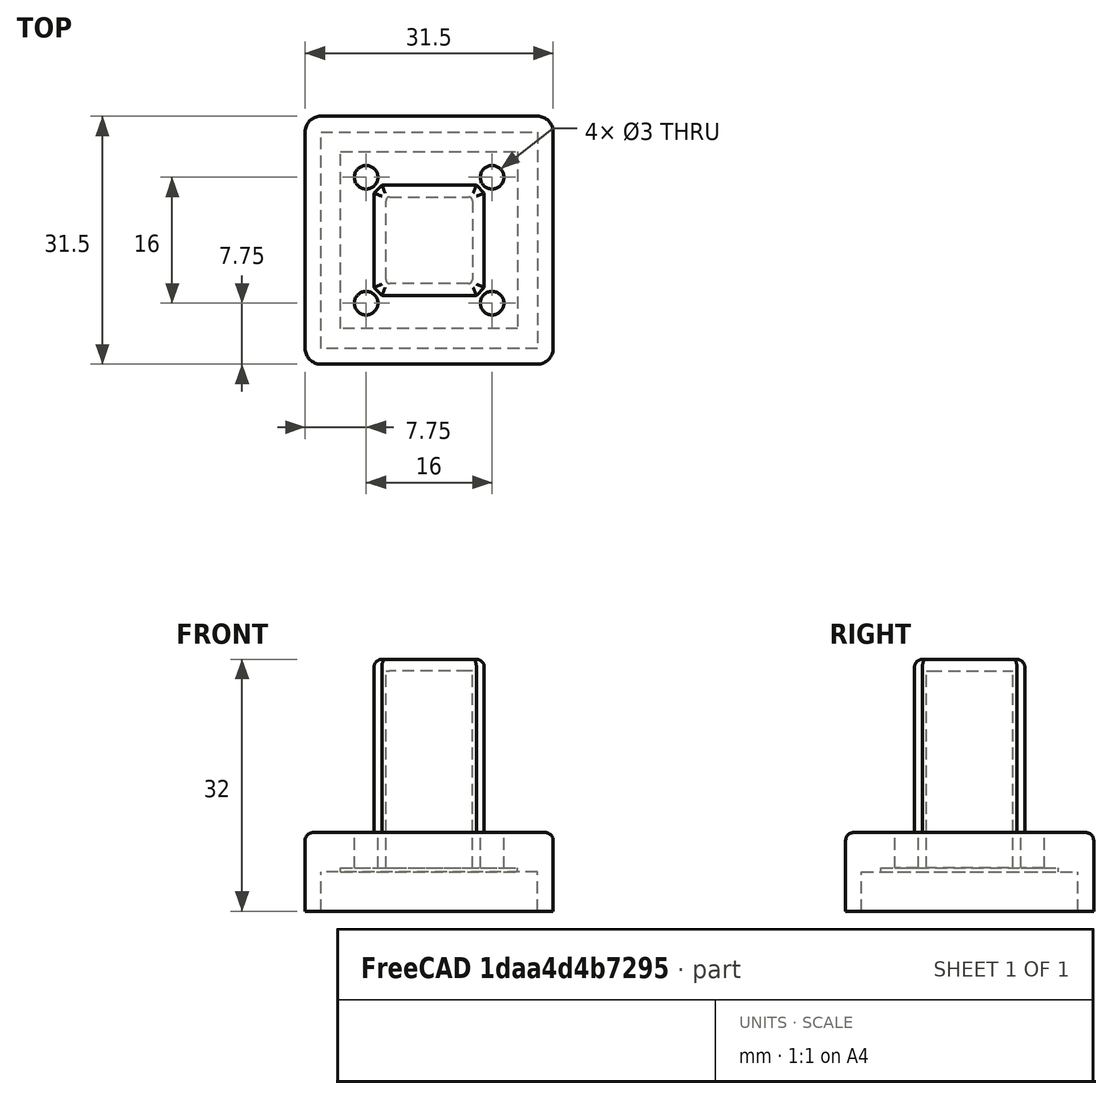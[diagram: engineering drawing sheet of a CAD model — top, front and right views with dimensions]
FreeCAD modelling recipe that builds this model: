
FCSTD DOCUMENT  (FreeCAD 1.1R44874 (Git))
Label: hood1slim_10x10x20_C
objects: Sketcher::SketchObject×7, PartDesign::Pocket×3, PartDesign::Pad×2, PartDesign::Fillet×2, App::Point×1, PartDesign::Hole×1, PartDesign::Body×1, Mesh::Feature×1
note: 39 computed .brp shape members not serialized (recipe doc carries the construction recipe); baked Part::Feature solids carry a one-line shape summary decoded from their .brp

FEATURE [App::Point] Origin001
  Role = Origin
FEATURE [Sketcher::SketchObject] Sketch
  ArcFitTolerance = 1e-06
  AttachmentSupport = -> [Origin]
  ExternalTypes = [0]
  FullyConstrained = true
  MakeInternals = false
  MapMode = 5
  _ExternalGeoVersion = 1
  sketch-geometry (13):
    g0: LineSegment StartX=-13.75 StartY=-15.75 StartZ=0 EndX=13.75 EndY=-15.75 EndZ=0
    g1: LineSegment StartX=15.75 StartY=-13.75 StartZ=0 EndX=15.75 EndY=13.75 EndZ=0
    g2: LineSegment StartX=13.75 StartY=15.75 StartZ=0 EndX=-13.75 EndY=15.75 EndZ=0
    g3: LineSegment StartX=-15.75 StartY=13.75 StartZ=0 EndX=-15.75 EndY=-13.75 EndZ=0
    g4: GeomPoint [constr] X=0 Y=0 Z=0
    g5: ArcOfCircle CenterX=-13.75 CenterY=13.75 CenterZ=0 NormalX=0 NormalY=0 NormalZ=1 AngleXU=0 Radius=2 StartAngle=1.5708 EndAngle=3.14159
    g6: GeomPoint [constr] X=-15.75 Y=15.75 Z=0
    g7: ArcOfCircle CenterX=13.75 CenterY=13.75 CenterZ=0 NormalX=0 NormalY=0 NormalZ=1 AngleXU=0 Radius=2 StartAngle=0 EndAngle=1.5708
    g8: GeomPoint [constr] X=15.75 Y=15.75 Z=0
    g9: ArcOfCircle CenterX=13.75 CenterY=-13.75 CenterZ=0 NormalX=0 NormalY=0 NormalZ=1 AngleXU=0 Radius=2 StartAngle=4.71239 EndAngle=6.28319
    g10: GeomPoint [constr] X=15.75 Y=-15.75 Z=0
    g11: ArcOfCircle CenterX=-13.75 CenterY=-13.75 CenterZ=0 NormalX=0 NormalY=0 NormalZ=1 AngleXU=0 Radius=2 StartAngle=3.14159 EndAngle=4.71239
    g12: GeomPoint [constr] X=-15.75 Y=-15.75 Z=0
  constraints (28):
    c: Horizontal(g0)
    c: Horizontal(g2)
    c: Vertical(g1)
    c: Vertical(g3)
    c: Symmetric(g8,g12,g4)
    c: Distance(g10,g12) = 31.5
    c: Distance(g12,g6) = 31.5
    c: Coincident(g4,g-1)
    c: PointOnObject(g6,g3)
    c: PointOnObject(g6,g2)
    c: Tangent(g3,g5) = -1.5708
    c: Tangent(g2,g5) = -1.5708
    c: Radius(g5) = 2
    c: PointOnObject(g8,g1)
    c: PointOnObject(g8,g2)
    c: Tangent(g1,g7) = -1.5708
    c: Tangent(g2,g7) = -1.5708
    c: PointOnObject(g10,g1)
    c: PointOnObject(g10,g0)
    c: Tangent(g1,g9) = -1.5708
    c: Tangent(g0,g9) = -1.5708
    c: PointOnObject(g12,g0)
    c: PointOnObject(g12,g3)
    c: Tangent(g0,g11) = -1.5708
    c: Tangent(g3,g11) = -1.5708
    c: Equal(g5,g7)
    c: Equal(g5,g11)
    c: Equal(g5,g9)
FEATURE [PartDesign::Pad] Pad
  Direction = (0,0,1)
  Length = 10
  Length2 = 10
  Profile = -> Sketch
  ReferenceAxis = -> Sketch [N_Axis]
  Refine = true
  SideType = 0
  Suppressed = false
  Type = 0
  Type2 = 0
FEATURE [Sketcher::SketchObject] Sketch001
  ArcFitTolerance = 1e-06
  AttachmentSupport = -> [Pad]
  ExternalTypes = [0]
  FullyConstrained = true
  MakeInternals = false
  MapMode = 5
  Placement = pos=(0,0,0) rot=(1,0,0;3.14159rad)
  _ExternalGeoVersion = 1
  sketch-geometry (5):
    g0: LineSegment StartX=-13.75 StartY=-13.75 StartZ=0 EndX=13.75 EndY=-13.75 EndZ=0
    g1: LineSegment StartX=13.75 StartY=-13.75 StartZ=0 EndX=13.75 EndY=13.75 EndZ=0
    g2: LineSegment StartX=13.75 StartY=13.75 StartZ=0 EndX=-13.75 EndY=13.75 EndZ=0
    g3: LineSegment StartX=-13.75 StartY=13.75 StartZ=0 EndX=-13.75 EndY=-13.75 EndZ=0
    g4: GeomPoint [constr] X=0 Y=0 Z=0
  constraints (12):
    c: Coincident(g0,g1)
    c: Coincident(g1,g2)
    c: Coincident(g2,g3)
    c: Coincident(g3,g0)
    c: Horizontal(g0)
    c: Horizontal(g2)
    c: Vertical(g1)
    c: Vertical(g3)
    c: Symmetric(g2,g0,g4)
    c: Distance(g1,g3) = 27.5
    c: Distance(g0,g2) = 27.5
    c: Coincident(g4,g-1)
FEATURE [PartDesign::Pocket] Pocket
  BaseFeature = -> Pad
  Direction = (0,0,1)
  Length = 5
  Length2 = 5
  Profile = -> Sketch001
  ReferenceAxis = -> Sketch001 [N_Axis]
  Refine = true
  SideType = 0
  Suppressed = false
  Type = 0
  Type2 = 0
FEATURE [Sketcher::SketchObject] Sketch002
  ArcFitTolerance = 1e-06
  AttachmentSupport = -> [Pocket]
  ExternalTypes = [0]
  FullyConstrained = true
  MakeInternals = false
  MapMode = 5
  Placement = pos=(0,0,5) rot=(1,0,0;3.14159rad)
  _ExternalGeoVersion = 1
  sketch-geometry (5):
    g0: LineSegment StartX=-11.25 StartY=-11.25 StartZ=0 EndX=11.25 EndY=-11.25 EndZ=0
    g1: LineSegment StartX=11.25 StartY=-11.25 StartZ=0 EndX=11.25 EndY=11.25 EndZ=0
    g2: LineSegment StartX=11.25 StartY=11.25 StartZ=0 EndX=-11.25 EndY=11.25 EndZ=0
    g3: LineSegment StartX=-11.25 StartY=11.25 StartZ=0 EndX=-11.25 EndY=-11.25 EndZ=0
    g4: GeomPoint [constr] X=0 Y=0 Z=0
  constraints (12):
    c: Coincident(g0,g1)
    c: Coincident(g1,g2)
    c: Coincident(g2,g3)
    c: Coincident(g3,g0)
    c: Horizontal(g0)
    c: Horizontal(g2)
    c: Vertical(g1)
    c: Vertical(g3)
    c: Symmetric(g2,g0,g4)
    c: Distance(g1,g3) = 22.5
    c: Distance(g0,g2) = 22.5
    c: Coincident(g4,g-1)
FEATURE [PartDesign::Pocket] Pocket001
  BaseFeature = -> Pocket
  Direction = (0,0,1)
  Length = 0.5
  Length2 = 5
  Profile = -> Sketch002
  ReferenceAxis = -> Sketch002 [N_Axis]
  Refine = true
  SideType = 0
  Suppressed = false
  Type = 0
  Type2 = 0
FEATURE [Sketcher::SketchObject] Sketch003
  ArcFitTolerance = 1e-06
  AttachmentSupport = -> [Pocket001]
  ExternalTypes = [0]
  FullyConstrained = true
  MakeInternals = false
  MapMode = 5
  Placement = pos=(0,0,5.5) rot=(1,0,0;3.14159rad)
  _ExternalGeoVersion = 1
  sketch-geometry (4):
    g0: Circle CenterX=8 CenterY=8 CenterZ=0 NormalX=0 NormalY=0 NormalZ=1 AngleXU=0 Radius=1.5
    g1: Circle CenterX=-8 CenterY=8 CenterZ=0 NormalX=0 NormalY=0 NormalZ=1 AngleXU=0 Radius=1.5
    g2: Circle CenterX=-8 CenterY=-8 CenterZ=0 NormalX=0 NormalY=0 NormalZ=1 AngleXU=0 Radius=1.5
    g3: Circle CenterX=8 CenterY=-8 CenterZ=0 NormalX=0 NormalY=0 NormalZ=1 AngleXU=0 Radius=1.5
  constraints (9):
    c: Diameter(g0) = 3
    c: DistanceY(g-1,g0) = 8
    c: DistanceX(g-1,g0) = 8
    c: Equal(g0,g1)
    c: Equal(g0,g2)
    c: Equal(g0,g3)
    c: Symmetric(g1,g3,g-1)
    c: Symmetric(g0,g3,g-1)
    c: Symmetric(g2,g3,g-2)
FEATURE [PartDesign::Hole] Hole
  BaseFeature = -> Pocket001
  BaseProfileType = 7
  CustomThreadClearance = 0
  Depth = 15
  DepthType = 0
  Diameter = 3
  DrillForDepth = false
  DrillPoint = 1
  DrillPointAngle = 118
  HoleCutCountersinkAngle = 90
  HoleCutCustomValues = false
  HoleCutDepth = 0
  HoleCutDiameter = 0
  HoleCutType = 0
  ModelThread = false
  Profile = -> Sketch003
  Refine = true
  Suppressed = false
  Tapered = false
  TaperedAngle = 90
  ThreadClass = 0
  ThreadDepth = 15
  ThreadDepthType = 0
  ThreadDiameter = 3
  ThreadDirection = 0
  ThreadFit = 0
  ThreadSize = 0
  ThreadType = 0
  Threaded = false
  UseCustomThreadClearance = false
FEATURE [Sketcher::SketchObject] Sketch004
  ArcFitTolerance = 1e-06
  AttachmentSupport = -> [Hole]
  ExternalGeometry = -> [Sketch002]
  ExternalTypes = [0,0,0,0]
  FullyConstrained = true
  MakeInternals = false
  MapMode = 5
  Placement = pos=(0,0,5.5) rot=(1,0,0;3.14159rad)
  _ExternalGeoVersion = 1
  sketch-geometry (21):
    g0: GeomPoint [constr] X=0 Y=0 Z=0
    g1: LineSegment StartX=-11.25 StartY=-5.5 StartZ=0 EndX=-11.25 EndY=5.5 EndZ=0
    g2: LineSegment StartX=-11.25 StartY=5.5 StartZ=0 EndX=-7 EndY=5.5 EndZ=0
    g3: LineSegment StartX=-5.5 StartY=7 StartZ=0 EndX=-5.5 EndY=11.25 EndZ=0
    g4: LineSegment StartX=-5.5 StartY=11.25 StartZ=0 EndX=5.5 EndY=11.25 EndZ=0
    g5: LineSegment StartX=5.5 StartY=11.25 StartZ=0 EndX=5.5 EndY=7 EndZ=0
    g6: LineSegment StartX=7 StartY=5.5 StartZ=0 EndX=11.25 EndY=5.5 EndZ=0
    g7: LineSegment StartX=11.25 StartY=5.5 StartZ=0 EndX=11.25 EndY=-5.5 EndZ=0
    g8: LineSegment StartX=11.25 StartY=-5.5 StartZ=0 EndX=7 EndY=-5.5 EndZ=0
    g9: LineSegment StartX=5.5 StartY=-7 StartZ=0 EndX=5.5 EndY=-11.25 EndZ=0
    g10: LineSegment StartX=5.5 StartY=-11.25 StartZ=0 EndX=-5.5 EndY=-11.25 EndZ=0
    g11: LineSegment StartX=-5.5 StartY=-11.25 StartZ=0 EndX=-5.5 EndY=-7 EndZ=0
    g12: LineSegment StartX=-7 StartY=-5.5 StartZ=0 EndX=-11.25 EndY=-5.5 EndZ=0
    g13: ArcOfCircle CenterX=-7 CenterY=7 CenterZ=0 NormalX=0 NormalY=0 NormalZ=1 AngleXU=0 Radius=1.5 StartAngle=4.71239 EndAngle=6.28319
    g14: GeomPoint [constr] X=-5.5 Y=5.5 Z=0
    g15: ArcOfCircle CenterX=7 CenterY=7 CenterZ=0 NormalX=0 NormalY=0 NormalZ=1 AngleXU=0 Radius=1.5 StartAngle=3.14159 EndAngle=4.71239
    g16: GeomPoint [constr] X=5.5 Y=5.5 Z=0
    g17: ArcOfCircle CenterX=7 CenterY=-7 CenterZ=0 NormalX=0 NormalY=0 NormalZ=1 AngleXU=0 Radius=1.5 StartAngle=1.5708 EndAngle=3.14159
    g18: GeomPoint [constr] X=5.5 Y=-5.5 Z=0
    g19: ArcOfCircle CenterX=-7 CenterY=-7 CenterZ=0 NormalX=0 NormalY=0 NormalZ=1 AngleXU=0 Radius=1.5 StartAngle=0 EndAngle=1.5708
    g20: GeomPoint [constr] X=-5.5 Y=-5.5 Z=0
  constraints (46):
    c: Coincident(g0,g-1)
    c: Coincident(g1,g2)
    c: Horizontal(g2)
    c: Vertical(g3)
    c: Coincident(g3,g4)
    c: Coincident(g4,g5)
    c: Vertical(g5)
    c: Horizontal(g6)
    c: Coincident(g6,g7)
    c: Coincident(g7,g8)
    c: Vertical(g9)
    c: Coincident(g9,g10)
    c: Coincident(g10,g11)
    c: Coincident(g12,g1)
    c: Tangent(g4,g-3)
    c: Tangent(g1,g-4)
    c: Tangent(g7,g-6)
    c: Tangent(g10,g-5)
    c: DistanceY(g-1,g16) = 5.5
    c: DistanceX(g-1,g16) = 5.5
    c: Symmetric(g16,g18,g-1)
    c: Symmetric(g16,g14,g-2)
    c: Symmetric(g18,g20,g-2)
    c: Parallel(g6,g8)
    c: Parallel(g2,g12)
    c: Parallel(g9,g11)
    c: PointOnObject(g14,g3)
    c: PointOnObject(g14,g2)
    c: Tangent(g3,g13) = -1.5708
    c: Tangent(g2,g13) = -1.5708
    c: Radius(g13) = 1.5
    c: PointOnObject(g16,g5)
    c: PointOnObject(g16,g6)
    c: Tangent(g5,g15) = -1.5708
    c: Tangent(g6,g15) = -1.5708
    c: PointOnObject(g18,g8)
    c: PointOnObject(g18,g9)
    c: Tangent(g8,g17) = -1.5708
    c: Tangent(g9,g17) = -1.5708
    c: PointOnObject(g20,g12)
    c: PointOnObject(g20,g11)
    c: Tangent(g12,g19) = -1.5708
    c: Tangent(g11,g19) = -1.5708
    c: Equal(g13,g15)
    c: Equal(g13,g19)
    c: Equal(g13,g17)
FEATURE [Sketcher::SketchObject] Sketch005
  ArcFitTolerance = 1e-06
  AttachmentSupport = -> [Hole]
  ExternalTypes = [0]
  FullyConstrained = true
  MakeInternals = false
  MapMode = 5
  Placement = pos=(0,0,10) rot=(0,0,1;0rad)
  _ExternalGeoVersion = 1
  sketch-geometry (17):
    g0: LineSegment StartX=-6 StartY=-7 StartZ=0 EndX=6 EndY=-7 EndZ=0
    g1: LineSegment StartX=7 StartY=-6 StartZ=0 EndX=7 EndY=6 EndZ=0
    g2: LineSegment StartX=6 StartY=7 StartZ=0 EndX=-6 EndY=7 EndZ=0
    g3: LineSegment StartX=-7 StartY=6 StartZ=0 EndX=-7 EndY=-6 EndZ=0
    g4: GeomPoint [constr] X=0 Y=0 Z=0
    g5: ArcOfCircle [constr] CenterX=-6 CenterY=6 CenterZ=0 NormalX=0 NormalY=0 NormalZ=1 AngleXU=0 Radius=1 StartAngle=1.5708 EndAngle=3.14159
    g6: GeomPoint [constr] X=-7 Y=7 Z=0
    g7: LineSegment StartX=-6 StartY=7 StartZ=0 EndX=-7 EndY=6 EndZ=0
    g8: ArcOfCircle [constr] CenterX=6 CenterY=-6 CenterZ=0 NormalX=0 NormalY=0 NormalZ=1 AngleXU=0 Radius=1 StartAngle=4.71239 EndAngle=6.28319
    g9: GeomPoint [constr] X=7 Y=-7 Z=0
    g10: LineSegment StartX=6 StartY=-7 StartZ=0 EndX=7 EndY=-6 EndZ=0
    g11: ArcOfCircle [constr] CenterX=6 CenterY=6 CenterZ=0 NormalX=0 NormalY=0 NormalZ=1 AngleXU=0 Radius=1 StartAngle=0 EndAngle=1.5708
    g12: GeomPoint [constr] X=7 Y=7 Z=0
    g13: LineSegment StartX=7 StartY=6 StartZ=0 EndX=6 EndY=7 EndZ=0
    g14: ArcOfCircle [constr] CenterX=-6 CenterY=-6 CenterZ=0 NormalX=0 NormalY=0 NormalZ=1 AngleXU=0 Radius=1 StartAngle=3.14159 EndAngle=4.71239
    g15: GeomPoint [constr] X=-7 Y=-7 Z=0
    g16: LineSegment StartX=-7 StartY=-6 StartZ=0 EndX=-6 EndY=-7 EndZ=0
  constraints (36):
    c: Horizontal(g0)
    c: Horizontal(g2)
    c: Vertical(g1)
    c: Vertical(g3)
    c: Symmetric(g12,g15,g4)
    c: Distance(g9,g15) = 14
    c: Distance(g15,g6) = 14
    c: Coincident(g4,g-1)
    c: PointOnObject(g6,g3)
    c: PointOnObject(g6,g2)
    c: Tangent(g3,g5) = -1.5708
    c: Tangent(g2,g5) = -1.5708
    c: Coincident(g7,g3)
    c: Coincident(g7,g2)
    c: PointOnObject(g9,g1)
    c: PointOnObject(g9,g0)
    c: Tangent(g1,g8) = -1.5708
    c: Tangent(g0,g8) = -1.5708
    c: Coincident(g10,g1)
    c: Coincident(g10,g0)
    c: Equal(g7,g10)
    c: DistanceY(g4,g3) = 6
    c: PointOnObject(g12,g2)
    c: PointOnObject(g12,g1)
    c: Tangent(g2,g11) = -1.5708
    c: Tangent(g1,g11) = -1.5708
    c: Coincident(g13,g2)
    c: Coincident(g13,g1)
    c: Equal(g7,g13)
    c: PointOnObject(g15,g0)
    c: PointOnObject(g15,g3)
    c: Tangent(g0,g14) = -1.5708
    c: Tangent(g3,g14) = -1.5708
    c: Coincident(g16,g0)
    c: Coincident(g16,g3)
    c: Equal(g7,g16)
FEATURE [PartDesign::Pad] Pad001
  BaseFeature = -> Hole
  Direction = (0,0,1)
  Length = 22
  Length2 = 10
  Profile = -> Sketch005
  ReferenceAxis = -> Sketch005 [N_Axis]
  Refine = true
  SideType = 0
  Suppressed = false
  Type = 0
  Type2 = 0
FEATURE [Sketcher::SketchObject] Sketch006
  ArcFitTolerance = 1e-06
  AttachmentSupport = -> [Pad001]
  ExternalTypes = [0]
  FullyConstrained = true
  MakeInternals = false
  MapMode = 5
  Placement = pos=(0,0,5.5) rot=(1,0,0;3.14159rad)
  _ExternalGeoVersion = 1
  sketch-geometry (10):
    g0: LineSegment StartX=-5 StartY=-5.5 StartZ=0 EndX=5 EndY=-5.5 EndZ=0
    g1: LineSegment StartX=5.5 StartY=-5 StartZ=0 EndX=5.5 EndY=5 EndZ=0
    g2: LineSegment StartX=5 StartY=5.5 StartZ=0 EndX=-5 EndY=5.5 EndZ=0
    g3: LineSegment StartX=-5.5 StartY=5 StartZ=0 EndX=-5.5 EndY=-5 EndZ=0
    g4: ArcOfCircle CenterX=-5 CenterY=-5 CenterZ=0 NormalX=0 NormalY=0 NormalZ=1 AngleXU=0 Radius=0.5 StartAngle=3.14159 EndAngle=4.71239
    g5: ArcOfCircle CenterX=5 CenterY=-5 CenterZ=0 NormalX=0 NormalY=0 NormalZ=1 AngleXU=0 Radius=0.5 StartAngle=4.71239 EndAngle=6.28319
    g6: ArcOfCircle CenterX=5 CenterY=5 CenterZ=0 NormalX=0 NormalY=0 NormalZ=1 AngleXU=0 Radius=0.5 StartAngle=0 EndAngle=1.5708
    g7: ArcOfCircle CenterX=-5 CenterY=5 CenterZ=0 NormalX=0 NormalY=0 NormalZ=1 AngleXU=0 Radius=0.5 StartAngle=1.5708 EndAngle=3.14159
    g8: GeomPoint [constr] X=5.5 Y=5.5 Z=0
    g9: GeomPoint [constr] X=0 Y=0 Z=0
  constraints (22):
    c: Tangent(g0,g4) = -1.5708
    c: Tangent(g0,g5) = -1.5708
    c: Tangent(g1,g5) = -1.5708
    c: Tangent(g1,g6) = -1.5708
    c: Tangent(g2,g6) = -1.5708
    c: Tangent(g2,g7) = -1.5708
    c: Tangent(g3,g7) = -1.5708
    c: Tangent(g3,g4) = -1.5708
    c: Horizontal(g0)
    c: Horizontal(g2)
    c: Vertical(g1)
    c: Vertical(g3)
    c: Equal(g4,g5)
    c: Equal(g5,g6)
    c: Equal(g6,g7)
    c: Symmetric(g2,g0,g9)
    c: PointOnObject(g8,g1)
    c: PointOnObject(g8,g2)
    c: Distance(g1,g3) = 11
    c: Distance(g0,g2) = 11
    c: Radius(g5) = 0.5
    c: Coincident(g9,g-1)
FEATURE [PartDesign::Pocket] Pocket002
  BaseFeature = -> Pad001
  Direction = (0,0,1)
  Length = 25
  Length2 = 5
  Profile = -> Sketch006
  ReferenceAxis = -> Sketch006 [N_Axis]
  Refine = true
  SideType = 0
  Suppressed = false
  Type = 0
  Type2 = 0
FEATURE [PartDesign::Fillet] Fillet
  Base = -> Pocket002 [Face29]
  BaseFeature = -> Pocket002
  Radius = 1
  Refine = true
  SupportTransform = false
  Suppressed = false
  UseAllEdges = false
FEATURE [PartDesign::Fillet] Fillet001
  Base = -> Fillet [Edge18]
  BaseFeature = -> Fillet
  Radius = 1
  Refine = true
  SupportTransform = false
  Suppressed = false
  UseAllEdges = false
FEATURE [PartDesign::Body] Body
  AllowCompound = true
  Group = -> [Sketch,Pad,Sketch001,Pocket,Sketch002,Pocket001,Sketch003,Hole,Sketch004,Sketch005,Pad001,Sketch006,Pocket002,Fillet,Fillet001]
  Origin = -> Origin
  Tip = -> Fillet001
FEATURE [Mesh::Feature] Mesh  label="Body (Meshed)"
